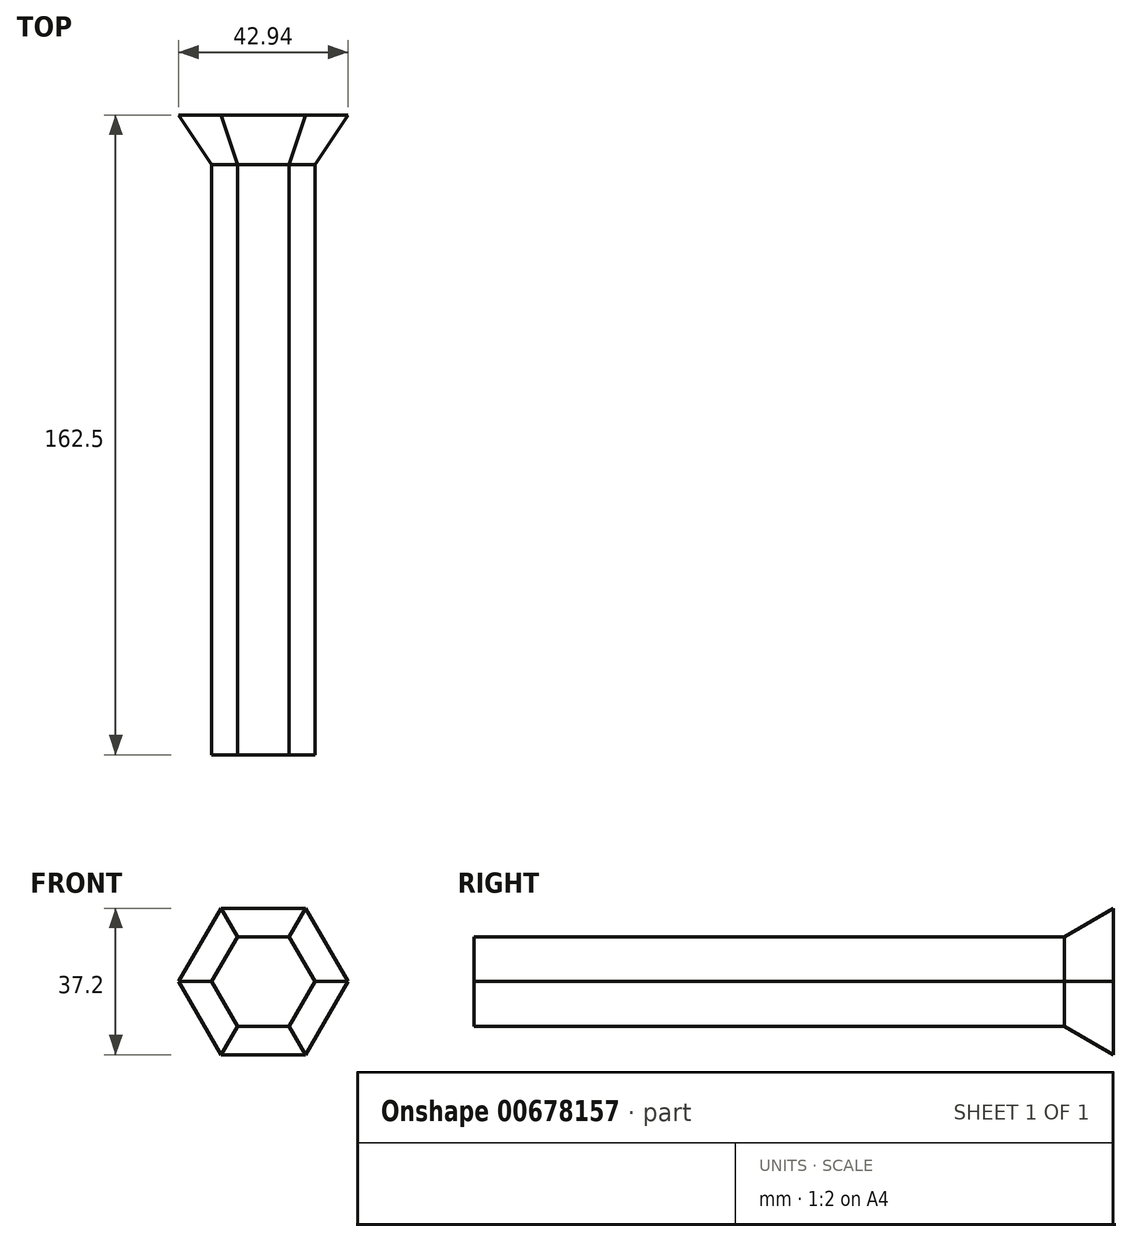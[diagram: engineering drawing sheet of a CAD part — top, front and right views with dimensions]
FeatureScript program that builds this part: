
annotation { "Feature Type Name" : "Feature", "Feature Type Description" : "" }
export const myFeature = defineFeature(function(context is Context, id is Id, definition is map)
    precondition{}
    {
        {
            var Q0;
            Q0=qCreatedBy(makeId("Front.planeOp"),FACE);
            var sketch = newSketch(context, id + "F0", { "sketchPlane" : qUnion([Q0])});
            skCircle(sketch, "E0.cCircle", {"center": v(0, 0) * mm, "radius": 11.38 * mm, "construction": true});
            skLineSegment(sketch, "E0.0", {"start": v(-6.57, 11.38) * mm, "end": v(6.57, 11.38) * mm});
            skLineSegment(sketch, "E0.1", {"start": v(6.57, 11.38) * mm, "end": v(13.14, 0) * mm});
            skLineSegment(sketch, "E0.2", {"start": v(13.14, 0) * mm, "end": v(6.57, -11.38) * mm});
            skLineSegment(sketch, "E0.3", {"start": v(6.57, -11.38) * mm, "end": v(-6.57, -11.38) * mm});
            skLineSegment(sketch, "E0.4", {"start": v(-6.57, -11.38) * mm, "end": v(-13.14, 0) * mm});
            skLineSegment(sketch, "E0.5", {"start": v(-13.14, 0) * mm, "end": v(-6.57, 11.38) * mm});
            skSolve(sketch);
        }
        {
            var Q0;
            Q0=makeQuery(id+"F0.imprint","IMPRINT",FACE,{"disambiguationData":[TD([[makeQuery(id+"F0.imprint","IMPRINT",EDGE,{"derivedFrom":sQuery(id+"F0.wireOp",EDGE,"E0.0")}),-1.0]])]});
            extrude(context, id + "F1", {"entities" : qUnion([Q0]), "depth" : 150 * mm, "offsetDistance" : 25 * mm});
        }
        {
            var Q0;
            Q0=makeQuery(id+"F0.imprint","IMPRINT",FACE,{"disambiguationData":[TD([[makeQuery(id+"F0.imprint","IMPRINT",EDGE,{"derivedFrom":sQuery(id+"F0.wireOp",EDGE,"E0.0")}),-1.0]])]});
            extrude(context, id + "F2", {"entities" : qUnion([Q0]), "operationType" : NewBodyOperationType.ADD, "oppositeDirection" : true, "depth" : 12.5 * mm, "offsetDistance" : 25 * mm, "hasDraft" : true, "draftAngle" : 30 * degree});
        }
    });
